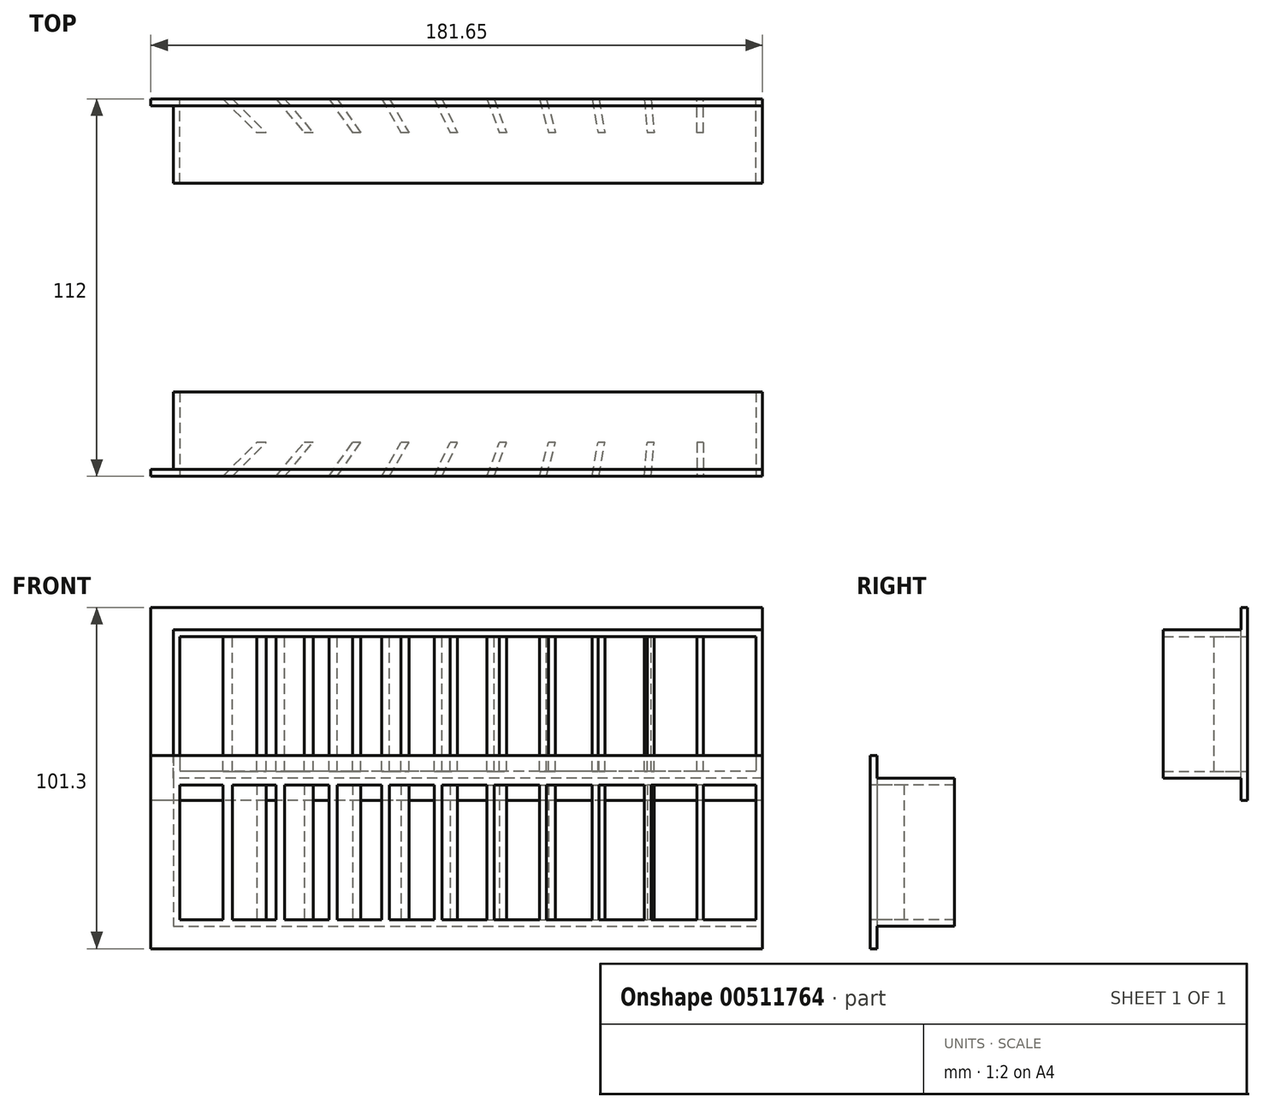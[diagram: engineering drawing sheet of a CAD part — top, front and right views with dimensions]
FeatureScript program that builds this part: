
annotation { "Feature Type Name" : "Feature", "Feature Type Description" : "" }
export const myFeature = defineFeature(function(context is Context, id is Id, definition is map)
    precondition{}
    {
        {
            var Q0;
            Q0=qCreatedBy(makeId("Front.planeOp"),FACE);
            var sketch = newSketch(context, id + "F0", { "sketchPlane" : qUnion([Q0])});
            skLineSegment(sketch, "E0.bottom", {"start": v(87.5, -22) * mm, "end": v(-87.5, -22) * mm});
            skLineSegment(sketch, "E0.top", {"start": v(87.5, 22) * mm, "end": v(-87.5, 22) * mm});
            skLineSegment(sketch, "E0.left", {"start": v(87.5, -22) * mm, "end": v(87.5, 22) * mm});
            skLineSegment(sketch, "E0.right", {"start": v(-87.5, -22) * mm, "end": v(-87.5, 22) * mm});
            skPoint(sketch, "E0.middle", {"position": v(0, 0) * mm});
            skLineSegment(sketch, "E1.0", {"start": v(85.5, 20) * mm, "end": v(-85.5, 20) * mm});
            skLineSegment(sketch, "E1.1", {"start": v(85.5, -20) * mm, "end": v(85.5, 20) * mm});
            skLineSegment(sketch, "E1.2", {"start": v(85.5, -20) * mm, "end": v(-85.5, -20) * mm});
            skLineSegment(sketch, "E1.3", {"start": v(-85.5, -20) * mm, "end": v(-85.5, 20) * mm});
            skSolve(sketch);
        }
        {
            var Q0;
            Q0 = qSketchRegion(id + "F0", true);
            extrude(context, id + "F1", {"entities" : qUnion([Q0]), "oppositeDirection" : true, "depth" : 25 * mm});
        }
        {
            var Q0;
            Q0=makeQuery(id+"F1.opExtrude","SWEPT_FACE",FACE,{"disambiguationData":[OSD([sQuery(id+"F0.wireOp",EDGE,"E1.2")])]});
            var sketch = newSketch(context, id + "F2", { "sketchPlane" : qUnion([Q0])});
            skLineSegment(sketch, "E2", {"start": v(85.5, 10) * mm, "end": v(-85.5, 10) * mm});
            skLineSegment(sketch, "E3", {"start": v(69.96, 10) * mm, "end": v(69.96, 0) * mm});
            skLineSegment(sketch, "E4", {"start": v(-23.28, 0) * mm, "end": v(-14.13, 15.85) * mm});
            skLineSegment(sketch, "E5", {"start": v(54.42, 0) * mm, "end": v(55.3, 10) * mm});
            skLineSegment(sketch, "E6", {"start": v(38.88, 0) * mm, "end": v(40.64, 10) * mm});
            skLineSegment(sketch, "E7", {"start": v(23.34, 0) * mm, "end": v(26.02, 10) * mm});
            skLineSegment(sketch, "E8", {"start": v(7.8, 0) * mm, "end": v(11.44, 10) * mm});
            skLineSegment(sketch, "E9", {"start": v(-7.74, 0) * mm, "end": v(-3.08, 10) * mm});
            skLineSegment(sketch, "E10.0", {"start": v(52.43, 0.17) * mm, "end": v(53.29, 10) * mm});
            skLineSegment(sketch, "E11.0", {"start": v(36.91, 0.35) * mm, "end": v(38.61, 10) * mm});
            skLineSegment(sketch, "E12", {"start": v(-38.82, 0) * mm, "end": v(-26.24, 17.96) * mm});
            skLineSegment(sketch, "E13", {"start": v(-54.36, 0) * mm, "end": v(-39.93, 17.2) * mm});
            skLineSegment(sketch, "E14", {"start": v(-69.9, 0) * mm, "end": v(-53.83, 16.07) * mm});
            skLineSegment(sketch, "E15.0", {"start": v(21.4, 0.52) * mm, "end": v(23.95, 10) * mm});
            skLineSegment(sketch, "E16.0", {"start": v(5.92, 0.68) * mm, "end": v(9.31, 10) * mm});
            skLineSegment(sketch, "E17.0", {"start": v(-9.55, 0.85) * mm, "end": v(-5.28, 10) * mm});
            skLineSegment(sketch, "E18", {"start": v(21.4, 0.52) * mm, "end": v(20.7, -2.12) * mm});
            skLineSegment(sketch, "E19", {"start": v(5.92, 0.68) * mm, "end": v(5.15, -1.44) * mm});
            skLineSegment(sketch, "E20", {"start": v(36.91, 0.35) * mm, "end": v(36.52, -1.84) * mm});
            skLineSegment(sketch, "E21", {"start": v(52.43, 0.17) * mm, "end": v(52.26, -1.75) * mm});
            skLineSegment(sketch, "E22", {"start": v(-9.55, 0.85) * mm, "end": v(-11.25, -2.8) * mm});
            skLineSegment(sketch, "E23.0", {"start": v(-25.01, 1) * mm, "end": v(-15.86, 16.85) * mm});
            skLineSegment(sketch, "E24.0", {"start": v(-40.46, 1.15) * mm, "end": v(-27.88, 19.1) * mm});
            skLineSegment(sketch, "E25.0", {"start": v(-55.9, 1.29) * mm, "end": v(-41.47, 18.48) * mm});
            skLineSegment(sketch, "E26.0", {"start": v(-71.31, 1.41) * mm, "end": v(-55.25, 17.48) * mm});
            skLineSegment(sketch, "E27", {"start": v(-25.01, 1) * mm, "end": v(-28.48, -5) * mm});
            skLineSegment(sketch, "E28", {"start": v(-40.46, 1.15) * mm, "end": v(-43.86, -3.7) * mm});
            skLineSegment(sketch, "E29", {"start": v(-55.9, 1.29) * mm, "end": v(-61.7, -5.62) * mm});
            skLineSegment(sketch, "E30", {"start": v(-71.31, 1.41) * mm, "end": v(-75.85, -3.13) * mm});
            skLineSegment(sketch, "E31.0", {"start": v(67.96, 10) * mm, "end": v(67.96, 0) * mm});
            skSolve(sketch);
        }
        {
            var Q0;
            {var subQ4=sQuery(id+"F2.wireOp",EDGE,"E8");Q0=makeQuery(id+"F2.imprint","IMPRINT",FACE,{"disambiguationData":[TD([[makeQuery(id+"F2.imprint","IMPRINT",EDGE,{"derivedFrom":subQ4}),1.0]])]});}
            var Q1;
            {var subQ4=sQuery(id+"F2.wireOp",EDGE,"E7");Q1=makeQuery(id+"F2.imprint","IMPRINT",FACE,{"disambiguationData":[TD([[makeQuery(id+"F2.imprint","IMPRINT",EDGE,{"derivedFrom":subQ4}),1.0]])]});}
            var Q2;
            {var subQ1=sQuery(id+"F2.wireOp",EDGE,"E6");Q2=makeQuery(id+"F2.imprint","IMPRINT",FACE,{"disambiguationData":[TD([[makeQuery(id+"F2.imprint","IMPRINT",EDGE,{"derivedFrom":subQ1}),1.0]])]});}
            var Q3;
            {var subQ4=sQuery(id+"F2.wireOp",EDGE,"E5");Q3=makeQuery(id+"F2.imprint","IMPRINT",FACE,{"disambiguationData":[TD([[makeQuery(id+"F2.imprint","IMPRINT",EDGE,{"derivedFrom":subQ4}),1.0]])]});}
            var Q4;
            {var subQ4=sQuery(id+"F2.wireOp",EDGE,"E9");Q4=makeQuery(id+"F2.imprint","IMPRINT",FACE,{"disambiguationData":[TD([[makeQuery(id+"F2.imprint","IMPRINT",EDGE,{"derivedFrom":subQ4}),1.0]])]});}
            var Q5;
            {var subQ5=sQuery(id+"F2.wireOp",EDGE,"E2");var subQ7=sQuery(id+"F2.wireOp",EDGE,"E4");var subQ9=makeQuery(id+"F2.imprint","INTERSECT",VERTEX,{"derivedFrom":[subQ5,subQ7]});Q5=makeQuery(id+"F2.imprint","IMPRINT",FACE,{"disambiguationData":[TD([[makeQuery(id+"F2.imprint","IMPRINT",EDGE,{"disambiguationData":[TD([[subQ9,-1.0]])],"derivedFrom":subQ5}),1.0]])]});}
            var Q6;
            {var subQ5=sQuery(id+"F2.wireOp",EDGE,"E2");var subQ7=sQuery(id+"F2.wireOp",EDGE,"E12");var subQ9=makeQuery(id+"F2.imprint","INTERSECT",VERTEX,{"derivedFrom":[subQ5,subQ7]});Q6=makeQuery(id+"F2.imprint","IMPRINT",FACE,{"disambiguationData":[TD([[makeQuery(id+"F2.imprint","IMPRINT",EDGE,{"disambiguationData":[TD([[subQ9,-1.0]])],"derivedFrom":subQ5}),1.0]])]});}
            var Q7;
            {var subQ3=sQuery(id+"F2.wireOp",EDGE,"E2");var subQ5=sQuery(id+"F2.wireOp",EDGE,"E13");var subQ8=makeQuery(id+"F2.imprint","INTERSECT",VERTEX,{"derivedFrom":[subQ3,subQ5]});Q7=makeQuery(id+"F2.imprint","IMPRINT",FACE,{"disambiguationData":[TD([[makeQuery(id+"F2.imprint","IMPRINT",EDGE,{"disambiguationData":[TD([[subQ8,-1.0]])],"derivedFrom":subQ3}),1.0]])]});}
            var Q8;
            {var subQ5=sQuery(id+"F2.wireOp",EDGE,"E14");var subQ7=sQuery(id+"F2.wireOp",EDGE,"E2");var subQ8=makeQuery(id+"F2.imprint","INTERSECT",VERTEX,{"derivedFrom":[subQ7,subQ5]});Q8=makeQuery(id+"F2.imprint","IMPRINT",FACE,{"disambiguationData":[TD([[makeQuery(id+"F2.imprint","IMPRINT",EDGE,{"disambiguationData":[TD([[subQ8,-1.0]])],"derivedFrom":subQ7}),1.0]])]});}
            var Q9;
            {var subQ0=sQuery(id+"F2.wireOp",EDGE,"E3");Q9=makeQuery(id+"F2.imprint","IMPRINT",FACE,{"disambiguationData":[TD([[makeQuery(id+"F2.imprint","IMPRINT",EDGE,{"derivedFrom":subQ0}),-1.0]])]});}
            var Q10;
            Q10=makeQuery(id+"F1.opExtrude","SWEPT_FACE",FACE,{"disambiguationData":[OSD([sQuery(id+"F0.wireOp",EDGE,"E1.0")])]});
            extrude(context, id + "F3", {"entities" : qUnion([Q0, Q1, Q2, Q3, Q4, Q5, Q6, Q7, Q8, Q9]), "operationType" : NewBodyOperationType.ADD, "endBound" : BoundingType.UP_TO_SURFACE, "endBoundEntityFace" : qUnion([Q10]), "depth" : 25 * mm});
        }
        {
            var Q0;
            Q0=makeQuery(id+"F1.opExtrude","SWEPT_FACE",FACE,{"disambiguationData":[OSD([sQuery(id+"F0.wireOp",EDGE,"E0.left")])]});
            var sketch = newSketch(context, id + "F4", { "sketchPlane" : qUnion([Q0])});
            skLineSegment(sketch, "E32.bottom", {"start": v(0, 22) * mm, "end": v(2, 22) * mm});
            skLineSegment(sketch, "E32.top", {"start": v(0, 28.65) * mm, "end": v(2, 28.65) * mm});
            skLineSegment(sketch, "E32.left", {"start": v(0, 22) * mm, "end": v(0, 28.65) * mm});
            skLineSegment(sketch, "E32.right", {"start": v(2, 22) * mm, "end": v(2, 28.65) * mm});
            skSolve(sketch);
        }
        {
            var Q0;
            Q0=makeQuery(id+"F4.imprint","IMPRINT",FACE,{"disambiguationData":[TD([[makeQuery(id+"F4.imprint","IMPRINT",EDGE,{"derivedFrom":sQuery(id+"F4.wireOp",EDGE,"E32.bottom")}),-1.0]])]});
            var Q1;
            Q1=makeQuery(id+"F1.opExtrude","CAP_EDGE",EDGE,{"disambiguationData":[OSD([sQuery(id+"F0.wireOp",EDGE,"E0.top")])],"isStart":true});
            var Q2;
            Q2=makeQuery(id+"F1.opExtrude","CAP_EDGE",EDGE,{"disambiguationData":[OSD([sQuery(id+"F0.wireOp",EDGE,"E0.right")])],"isStart":true});
            var Q3;
            Q3=makeQuery(id+"F1.opExtrude","CAP_EDGE",EDGE,{"disambiguationData":[OSD([sQuery(id+"F0.wireOp",EDGE,"E0.bottom")])],"isStart":true});
            sweep(context, id + "F5", {"operationType" : NewBodyOperationType.ADD, "profiles" : qUnion([Q0]), "path" : qUnion([Q1, Q2, Q3])});
        }
        {
            var Q0;
            Q0=makeQuery(id+"F1.opExtrude","SWEPT_BODY",BODY,{"disambiguationData":[OSD([sQuery(id+"F0.wireOp",EDGE,"E0.bottom"),sQuery(id+"F0.wireOp",EDGE,"E0.top"),sQuery(id+"F0.wireOp",EDGE,"E0.left"),sQuery(id+"F0.wireOp",EDGE,"E0.right"),sQuery(id+"F0.wireOp",EDGE,"E1.0"),sQuery(id+"F0.wireOp",EDGE,"E1.1"),sQuery(id+"F0.wireOp",EDGE,"E1.2"),sQuery(id+"F0.wireOp",EDGE,"E1.3")])]});
            transform(context, id + "F6", {"entities" : qUnion([Q0]), "transformType" : TransformType.TRANSLATION_3D, "dx" : 0 * mm, "dy" : 62 * mm, "dz" : 0 * mm, "makeCopy" : true});
        }
        {
            var Q0;
            Q0=makeQuery(id+"F6.opPattern","COPY",BODY,{"derivedFrom":makeQuery(id+"F1.opExtrude","SWEPT_BODY",BODY,{"disambiguationData":[OSD([sQuery(id+"F0.wireOp",EDGE,"E0.bottom"),sQuery(id+"F0.wireOp",EDGE,"E0.top"),sQuery(id+"F0.wireOp",EDGE,"E0.left"),sQuery(id+"F0.wireOp",EDGE,"E0.right"),sQuery(id+"F0.wireOp",EDGE,"E1.0"),sQuery(id+"F0.wireOp",EDGE,"E1.1"),sQuery(id+"F0.wireOp",EDGE,"E1.2"),sQuery(id+"F0.wireOp",EDGE,"E1.3")])]}),"instanceName":"1"});
            var Q1;
            Q1=makeQuery(id+"F6.opPattern","COPY",EDGE,{"derivedFrom":makeQuery(id+"F1.opExtrude","CAP_EDGE",EDGE,{"disambiguationData":[OSD([sQuery(id+"F0.wireOp",EDGE,"E0.top")])],"isStart":false}),"instanceName":"1"});
            transform(context, id + "F7", {"entities" : qUnion([Q0]), "transformType" : TransformType.ROTATION, "transformAxis" : qUnion([Q1]), "angle" : 180 * degree, "makeCopy" : false});
        }
    });
